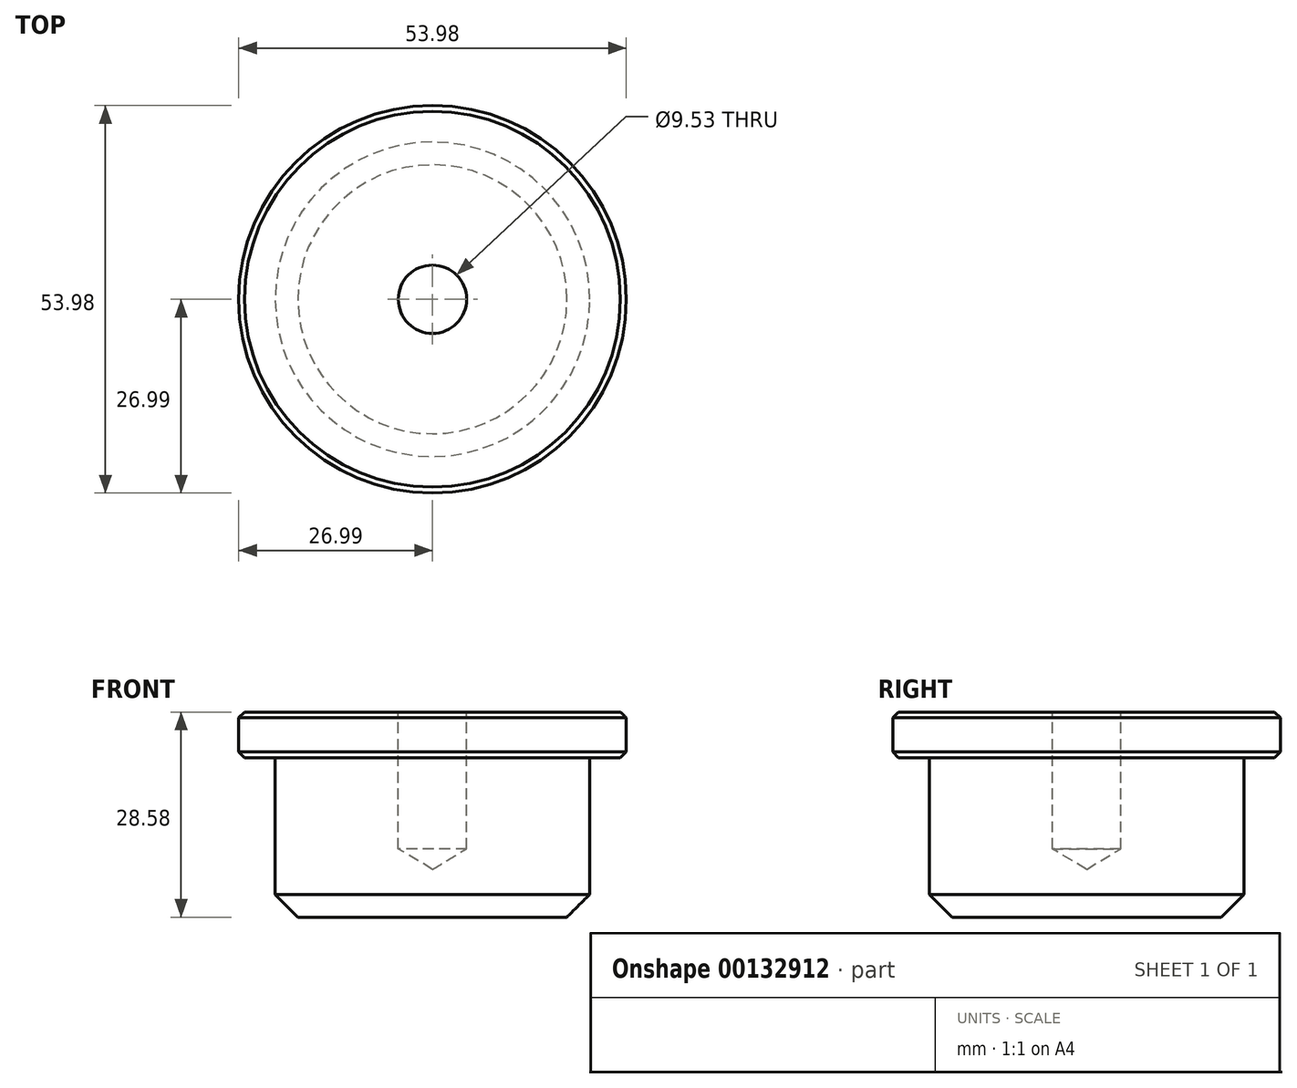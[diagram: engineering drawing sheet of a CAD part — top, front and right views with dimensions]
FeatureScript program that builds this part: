
annotation { "Feature Type Name" : "Feature", "Feature Type Description" : "" }
export const myFeature = defineFeature(function(context is Context, id is Id, definition is map)
    precondition{}
    {
        {
            var Q0;
            Q0=qCreatedBy(makeId("Top.planeOp"),FACE);
            var sketch = newSketch(context, id + "F0", { "sketchPlane" : qUnion([Q0])});
            skCircle(sketch, "E0", {"center": v(0, 0) * mm, "radius": 21.9 * mm});
            skCircle(sketch, "E1", {"center": v(0, 0) * mm, "radius": 26.99 * mm});
            skSolve(sketch);
        }
        {
            var Q0;
            Q0=makeQuery(id+"F0.imprint","IMPRINT",FACE,{"disambiguationData":[TD([[makeQuery(id+"F0.imprint","IMPRINT",EDGE,{"derivedFrom":sQuery(id+"F0.wireOp",EDGE,"E0")}),1.0]])]});
            extrude(context, id + "F1", {"entities" : qUnion([Q0]), "oppositeDirection" : true, "depth" : 22.22 * mm});
        }
        {
            var Q0;
            Q0=makeQuery(id+"F0.imprint","IMPRINT",FACE,{"disambiguationData":[TD([[makeQuery(id+"F0.imprint","IMPRINT",EDGE,{"derivedFrom":sQuery(id+"F0.wireOp",EDGE,"E0")}),1.0]])]});
            var Q1;
            Q1=makeQuery(id+"F0.imprint","IMPRINT",FACE,{"disambiguationData":[TD([[makeQuery(id+"F0.imprint","IMPRINT",EDGE,{"derivedFrom":sQuery(id+"F0.wireOp",EDGE,"E0")}),-1.0]])]});
            extrude(context, id + "F2", {"entities" : qUnion([Q0, Q1]), "operationType" : NewBodyOperationType.ADD, "depth" : 6.35 * mm});
        }
        {
            var Q0;
            Q0=makeQuery(id+"F1.opExtrude","CAP_EDGE",EDGE,{"disambiguationData":[OSD([sQuery(id+"F0.wireOp",EDGE,"E0")])],"isStart":false});
            chamfer(context, id + "F3", {"entities" : qUnion([Q0]), "width" : 3.17 * mm, "tangentPropagation" : true});
        }
        {
            var Q0;
            Q0=makeQuery(id+"F2.opExtrude","CAP_EDGE",EDGE,{"disambiguationData":[OSD([sQuery(id+"F0.wireOp",EDGE,"E1")])],"isStart":true});
            var Q1;
            Q1=makeQuery(id+"F2.opExtrude","CAP_EDGE",EDGE,{"disambiguationData":[OSD([sQuery(id+"F0.wireOp",EDGE,"E1")])],"isStart":false});
            chamfer(context, id + "F4", {"entities" : qUnion([Q0, Q1]), "width" : 0.81 * mm, "tangentPropagation" : true});
        }
        {
            var Q0;
            Q0=makeQuery(id+"F2.opExtrude","CAP_FACE",FACE,{"disambiguationData":[OSD([sQuery(id+"F0.wireOp",EDGE,"E1")])],"isStart":false});
            var sketch = newSketch(context, id + "F5", { "sketchPlane" : qUnion([Q0])});
            skPoint(sketch, "E2", {"position": v(0, 0) * mm});
            skSolve(sketch);
        }
        {
            var Q0;
            Q0=sQuery(id+"F5.wireOp",VERTEX,"E2");
            var Q1;
            Q1=makeQuery(id+"F1.opExtrude","SWEPT_BODY",BODY,{"disambiguationData":[OSD([sQuery(id+"F0.wireOp",EDGE,"E0")])]});
            hole(context, id + "F6", {"style" : HoleStyle.SIMPLE, "endStyle" : HoleEndStyle.BLIND, "holeDiameter" : 9.52 * mm, "holeDepth" : 19.05 * mm, "locations" : qUnion([Q0]), "scope" : qUnion([Q1])});
        }
    });
